# Revit family: IS_Connect_E7913_BIM_NL
name_source: partatom
category: Plumbing Fixtures
revit_build: Autodesk Revit MEP 2014 (Build: 20130308_1515(x64)
units: mm (PartAtom-declared; Revit-internal decimal feet)

## types (2) — shared parameters
AreaUnits = millimeters
Assembly Code = C1030200
Brand = Ideal Standard
Default Elevation = 800 mm  [stored 2.62467 ft]
ECA = No
IfcExportAs = IfcSanitaryType
IfcExportType = WASHHANDBASIN
LinearUnits = millimeters
NominalDepth = 262 mm  [stored 0.85958 ft]
NominalHeight = 153 mm
NominalLength = 262 mm  [stored 0.85958 ft]
NominalWidth = 350 mm
Size = 350 x 262 x 153 mm
URL = www.idealstandardnederland.nl
Uniclass2015Version = Products v1.1
Version = 1
VolumeUnits = liter
WRAS = No
WarrantyDescription = Fabrieksgarantie
WarrantyDurationUnit = jaar
WaterEfficientProduct = No
zero-valued in all types: CWFU, Cost, DrainSize, HWFU, WFU

## per-type parameters (varying)
| type | BIMObjectName | Model | ModelNumber | NBSDescription | NBSReference | Name | Uniclass2015Code | Uniclass2015Title |
| E791301 - Connect | ISI_IdealStandard_Wall-HungHandRinseBasins_E791301 | E791301 | E791301 | Wall-hung hand rinse basins | 45-35-70/368 | Wall-HungHandRinseBasins_E791301_IdealStandard | Pr_40_20_96_95 | Wall-hung hand rinse basins |
| Add Product Code and Short Description here | ISI_IdealStandard_Wall-HungWashBasins_ |  |  | Wall-hung wash basins | 45-35-70/369 | Wall-HungWashBasins__IdealStandard | Pr_40_20_96_96 | Wall-hung wash basins |

note: [stored X ft] marks values corroborated as IEEE doubles in the binary element streams (Revit-internal decimal feet)

## geometry (parser evidence)
native form markers: Sweep x2
no freeform markers — native parametric forms only
